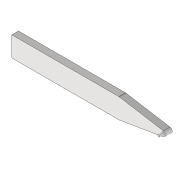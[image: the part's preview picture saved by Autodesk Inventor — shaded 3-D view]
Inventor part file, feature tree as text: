
AUTODESK INVENTOR PART (.ipt)
format: ipt  version: 2020 (Build 240168000, 168)  size: 93,184 bytes
history: native  units: mm
features: extrude x2, sketch x2
ambient origin geometry x8: Origin, YZ Plane, XZ Plane, XY Plane, X Axis, Y Axis, Z Axis, Center Point
bodies: Volumenkörper1 (feature_tree)
feature tree (4):
  extrude  "Extrusion1"  Depth=2.0mm
  extrude  "Extrusion2"  Depth=15.0mm
  sketch  "Skizze1"  dims[d0=2.0mm d1=2.0mm]
  sketch  "Skizze2"  dims[d2=115.0mm d3=80.0mm d4=5.0mm d5=0.0mm d6=2.5mm d7=3.0mm d8=-1.745329mm d9=15.0mm]
